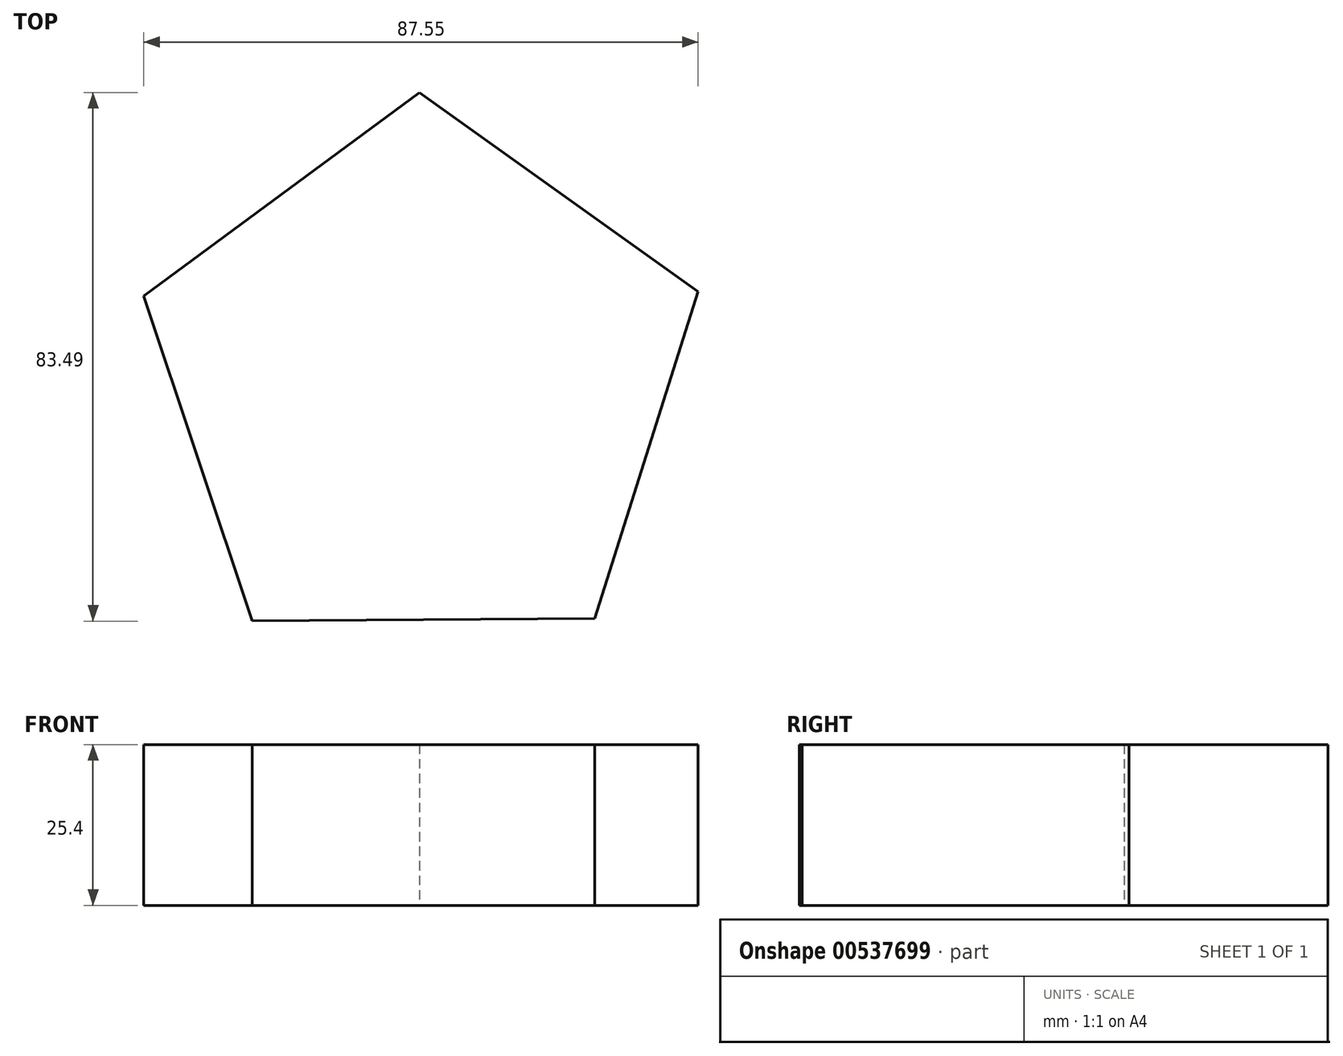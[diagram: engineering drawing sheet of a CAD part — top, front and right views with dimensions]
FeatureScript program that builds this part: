
annotation { "Feature Type Name" : "Feature", "Feature Type Description" : "" }
export const myFeature = defineFeature(function(context is Context, id is Id, definition is map)
    precondition{}
    {
        {
            var Q0;
            Q0=qCreatedBy(makeId("Top.planeOp"),FACE);
            var sketch = newSketch(context, id + "F0", { "sketchPlane" : qUnion([Q0])});
            skCircle(sketch, "E0.cCircle", {"center": v(0, 0) * mm, "radius": 46.03 * mm, "construction": true});
            skLineSegment(sketch, "E0.0", {"start": v(-43.9, 13.87) * mm, "end": v(-0.37, 46.03) * mm});
            skLineSegment(sketch, "E0.1", {"start": v(-0.37, 46.03) * mm, "end": v(43.66, 14.58) * mm});
            skLineSegment(sketch, "E0.2", {"start": v(43.66, 14.58) * mm, "end": v(27.36, -37.02) * mm});
            skLineSegment(sketch, "E0.3", {"start": v(27.36, -37.02) * mm, "end": v(-26.75, -37.46) * mm});
            skLineSegment(sketch, "E0.4", {"start": v(-26.75, -37.46) * mm, "end": v(-43.9, 13.87) * mm});
            skSolve(sketch);
        }
        {
            var Q0;
            Q0=makeQuery(id+"F0.imprint","IMPRINT",FACE,{"disambiguationData":[TD([[makeQuery(id+"F0.imprint","IMPRINT",EDGE,{"derivedFrom":sQuery(id+"F0.wireOp",EDGE,"E0.0")}),-1.0]])]});
            extrude(context, id + "F1", {"entities" : qUnion([Q0]), "depth" : 25.4 * mm, "offsetDistance" : 25.4 * mm});
        }
    });
